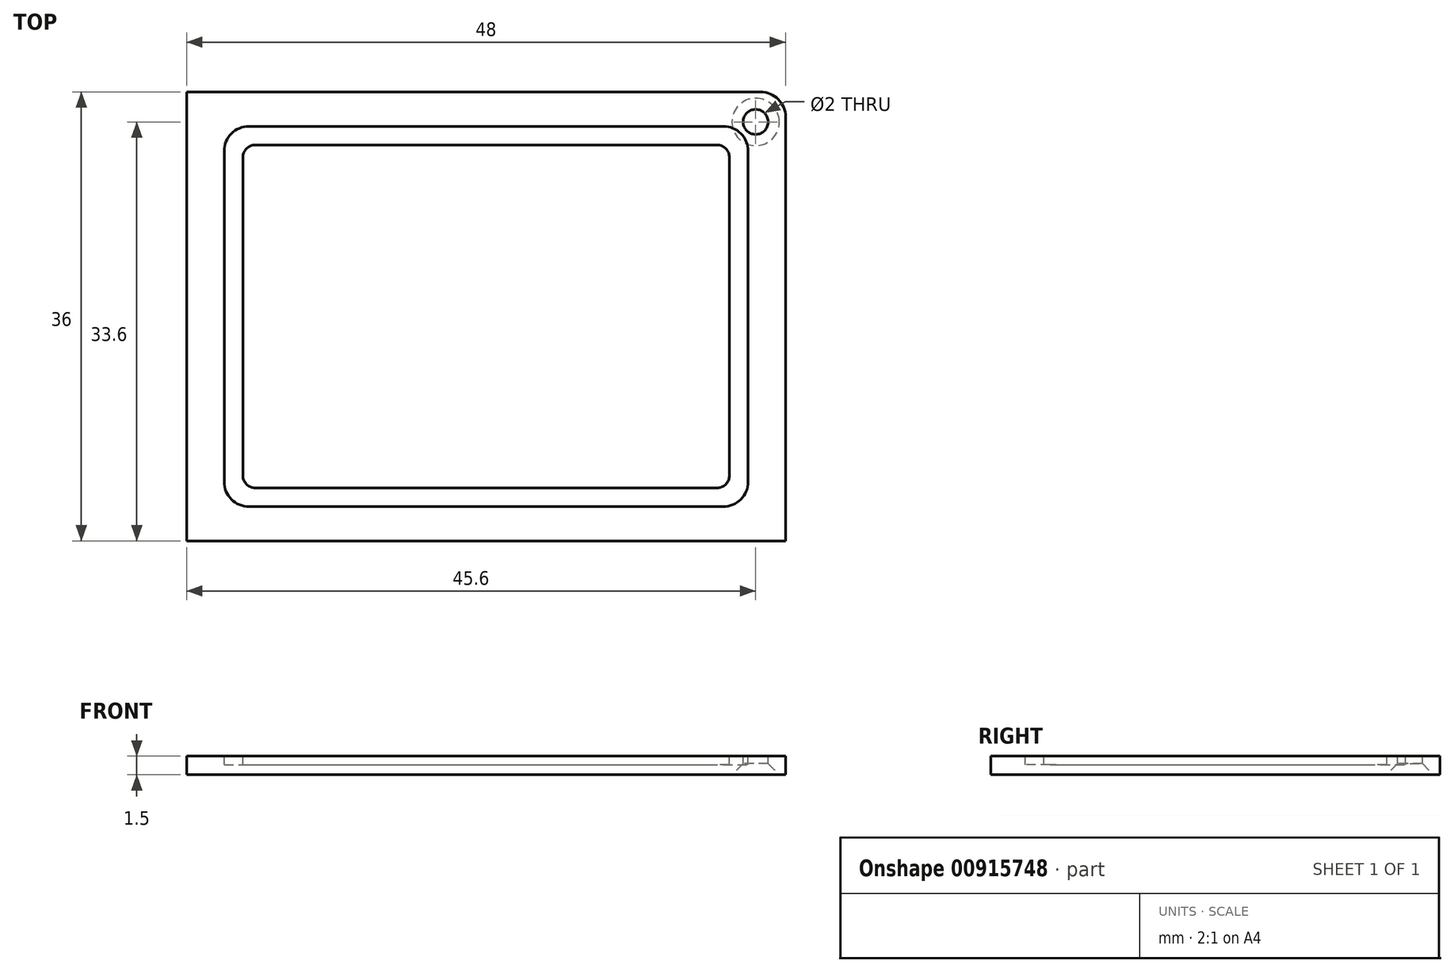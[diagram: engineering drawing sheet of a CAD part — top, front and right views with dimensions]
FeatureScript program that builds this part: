
annotation { "Feature Type Name" : "Feature", "Feature Type Description" : "" }
export const myFeature = defineFeature(function(context is Context, id is Id, definition is map)
    precondition{}
    {
        {
            var Q0;
            Q0=qCreatedBy(makeId("Top.planeOp"),FACE);
            var sketch = newSketch(context, id + "F0", { "sketchPlane" : qUnion([Q0])});
            skLineSegment(sketch, "E0.bottom", {"start": v(0, 0) * mm, "end": v(38, 0) * mm, "construction": true});
            skLineSegment(sketch, "E0.top", {"start": v(0, 26.5) * mm, "end": v(38, 26.5) * mm, "construction": true});
            skLineSegment(sketch, "E0.left", {"start": v(0, 0) * mm, "end": v(0, 26.5) * mm, "construction": true});
            skLineSegment(sketch, "E0.right", {"start": v(38, 0) * mm, "end": v(38, 26.5) * mm, "construction": true});
            skSolve(sketch);
        }
        {
            var Q0;
            Q0=qCreatedBy(makeId("Top.planeOp"),FACE);
            var sketch = newSketch(context, id + "F1", { "sketchPlane" : qUnion([Q0])});
            skLineSegment(sketch, "E1.bottom", {"start": v(-5, -4.75) * mm, "end": v(43, -4.75) * mm});
            skLineSegment(sketch, "E1.top", {"start": v(-5, 31.25) * mm, "end": v(43, 31.25) * mm});
            skLineSegment(sketch, "E1.left", {"start": v(-5, -4.75) * mm, "end": v(-5, 31.25) * mm});
            skLineSegment(sketch, "E1.right", {"start": v(43, -4.75) * mm, "end": v(43, 31.25) * mm});
            skSolve(sketch);
        }
        {
            var Q0;
            Q0=makeQuery(id+"F1.imprint","IMPRINT",FACE,{"disambiguationData":[TD([[makeQuery(id+"F1.imprint","IMPRINT",EDGE,{"derivedFrom":sQuery(id+"F1.wireOp",EDGE,"E1.bottom")}),1.0]])]});
            extrude(context, id + "F2", {"entities" : qUnion([Q0]), "depth" : 1.5 * mm, "offsetDistance" : 25 * mm});
        }
        {
            var Q0;
            Q0=makeQuery(id+"F2.opExtrude","CAP_FACE",FACE,{"disambiguationData":[OSD([sQuery(id+"F1.wireOp",EDGE,"E1.bottom"),sQuery(id+"F1.wireOp",EDGE,"E1.top"),sQuery(id+"F1.wireOp",EDGE,"E1.left"),sQuery(id+"F1.wireOp",EDGE,"E1.right")])],"isStart":false});
            var sketch = newSketch(context, id + "F3", { "sketchPlane" : qUnion([Q0])});
            skLineSegment(sketch, "E2.bottom", {"start": v(-0.5, -0.5) * mm, "end": v(38.5, -0.5) * mm});
            skLineSegment(sketch, "E2.top", {"start": v(-0.5, 27) * mm, "end": v(38.5, 27) * mm});
            skLineSegment(sketch, "E2.left", {"start": v(-0.5, -0.5) * mm, "end": v(-0.5, 27) * mm});
            skLineSegment(sketch, "E2.right", {"start": v(38.5, -0.5) * mm, "end": v(38.5, 27) * mm});
            skSolve(sketch);
        }
        {
            var Q0;
            Q0=makeQuery(id+"F3.imprint","IMPRINT",FACE,{"disambiguationData":[TD([[makeQuery(id+"F3.imprint","IMPRINT",EDGE,{"derivedFrom":sQuery(id+"F3.wireOp",EDGE,"E2.bottom")}),-1.0]])]});
            var sketch = newSketch(context, id + "F4", { "sketchPlane" : qUnion([Q0])});
            skLineSegment(sketch, "E3.0", {"start": v(-2, 28.5) * mm, "end": v(40, 28.5) * mm});
            skLineSegment(sketch, "E3.1", {"start": v(-2, -2) * mm, "end": v(-2, 28.5) * mm});
            skLineSegment(sketch, "E3.2", {"start": v(-2, -2) * mm, "end": v(40, -2) * mm});
            skLineSegment(sketch, "E3.3", {"start": v(40, -2) * mm, "end": v(40, 28.5) * mm});
            skSolve(sketch);
        }
        {
            var Q0;
            Q0=makeQuery(id+"F4.imprint","IMPRINT",FACE,{"disambiguationData":[TD([[makeQuery(id+"F4.imprint","IMPRINT",EDGE,{"derivedFrom":sQuery(id+"F4.wireOp",EDGE,"E3.0")}),1.0]])]});
            var sketch = newSketch(context, id + "F5", { "sketchPlane" : qUnion([Q0])});
            skCircle(sketch, "E4", {"center": v(40.6, 28.85) * mm, "radius": 1.9 * mm});
            skCircle(sketch, "E5", {"center": v(40.6, 28.85) * mm, "radius": 1 * mm});
            skSolve(sketch);
        }
        {
            var Q0;
            Q0=makeQuery(id+"F4.imprint","IMPRINT",FACE,{"disambiguationData":[TD([[makeQuery(id+"F4.imprint","IMPRINT",EDGE,{"derivedFrom":sQuery(id+"F4.wireOp",EDGE,"E3.0")}),-1.0]])]});
            extrude(context, id + "F6", {"entities" : qUnion([Q0]), "operationType" : NewBodyOperationType.REMOVE, "oppositeDirection" : true, "depth" : .7 * mm, "offsetDistance" : 25 * mm});
        }
        {
            var Q0;
            Q0=makeQuery(id+"F6.boolean.opBoolean","COPY",EDGE,{"derivedFrom":makeQuery(id+"F6.opExtrude","SWEPT_EDGE",EDGE,{"disambiguationData":[OSD([sQuery(id+"F4.wireOp",EDGE,"E3.0"),sQuery(id+"F4.wireOp",EDGE,"E3.3")])]})});
            var Q1;
            Q1=makeQuery(id+"F6.boolean.opBoolean","COPY",EDGE,{"derivedFrom":makeQuery(id+"F6.opExtrude","SWEPT_EDGE",EDGE,{"disambiguationData":[OSD([sQuery(id+"F4.wireOp",EDGE,"E3.2"),sQuery(id+"F4.wireOp",EDGE,"E3.3")])]})});
            var Q2;
            Q2=makeQuery(id+"F6.boolean.opBoolean","COPY",EDGE,{"derivedFrom":makeQuery(id+"F6.opExtrude","SWEPT_EDGE",EDGE,{"disambiguationData":[OSD([sQuery(id+"F4.wireOp",EDGE,"E3.0"),sQuery(id+"F4.wireOp",EDGE,"E3.1")])]})});
            var Q3;
            Q3=makeQuery(id+"F6.boolean.opBoolean","COPY",EDGE,{"derivedFrom":makeQuery(id+"F6.opExtrude","SWEPT_EDGE",EDGE,{"disambiguationData":[OSD([sQuery(id+"F4.wireOp",EDGE,"E3.1"),sQuery(id+"F4.wireOp",EDGE,"E3.2")])]})});
            fillet(context, id + "F7", {"entities" : qUnion([Q0, Q1, Q2, Q3]), "radius" : 2 * mm, "tangentPropagation" : true, "allowEdgeOverflow" : false});
        }
        {
            var Q0;
            Q0=makeQuery(id+"F6.boolean.opBoolean","COPY",EDGE,{"derivedFrom":makeQuery(id+"F6.opExtrude","SWEPT_EDGE",EDGE,{"disambiguationData":[OSD([sQuery(id+"F3.wireOp",EDGE,"E2.top"),sQuery(id+"F3.wireOp",EDGE,"E2.right")])]})});
            var Q1;
            Q1=makeQuery(id+"F6.boolean.opBoolean","COPY",EDGE,{"derivedFrom":makeQuery(id+"F6.opExtrude","SWEPT_EDGE",EDGE,{"disambiguationData":[OSD([sQuery(id+"F3.wireOp",EDGE,"E2.bottom"),sQuery(id+"F3.wireOp",EDGE,"E2.right")])]})});
            var Q2;
            Q2=makeQuery(id+"F6.boolean.opBoolean","COPY",EDGE,{"derivedFrom":makeQuery(id+"F6.opExtrude","SWEPT_EDGE",EDGE,{"disambiguationData":[OSD([sQuery(id+"F3.wireOp",EDGE,"E2.bottom"),sQuery(id+"F3.wireOp",EDGE,"E2.left")])]})});
            var Q3;
            Q3=makeQuery(id+"F6.boolean.opBoolean","COPY",EDGE,{"derivedFrom":makeQuery(id+"F6.opExtrude","SWEPT_EDGE",EDGE,{"disambiguationData":[OSD([sQuery(id+"F3.wireOp",EDGE,"E2.top"),sQuery(id+"F3.wireOp",EDGE,"E2.left")])]})});
            fillet(context, id + "F8", {"entities" : qUnion([Q0, Q1, Q2, Q3]), "radius" : 1 * mm, "tangentPropagation" : true, "allowEdgeOverflow" : false});
        }
        {
            var Q0;
            Q0=makeQuery(id+"F5.imprint","IMPRINT",FACE,{"disambiguationData":[TD([[makeQuery(id+"F5.imprint","IMPRINT",EDGE,{"derivedFrom":sQuery(id+"F5.wireOp",EDGE,"E5")}),1.0]])]});
            extrude(context, id + "F9", {"entities" : qUnion([Q0]), "operationType" : NewBodyOperationType.REMOVE, "oppositeDirection" : true, "depth" : 25 * mm, "offsetDistance" : 25 * mm});
        }
        {
            var Q0;
            Q0=makeQuery(id+"F9.boolean.opBoolean","INTERSECT",EDGE,{"derivedFrom":[makeQuery(id+"F2.opExtrude","CAP_FACE",FACE,{"disambiguationData":[OSD([sQuery(id+"F1.wireOp",EDGE,"E1.bottom"),sQuery(id+"F1.wireOp",EDGE,"E1.top"),sQuery(id+"F1.wireOp",EDGE,"E1.left"),sQuery(id+"F1.wireOp",EDGE,"E1.right")])],"isStart":true}),makeQuery(id+"F9.opExtrude","SWEPT_FACE",FACE,{"disambiguationData":[OSD([sQuery(id+"F5.wireOp",EDGE,"E5")])]})]});
            chamfer(context, id + "F10", {"entities" : qUnion([Q0]), "chamferType" : ChamferType.OFFSET_ANGLE, "width" : .9 * mm, "oppositeDirection" : false, "angle" : 45 * degree, "tangentPropagation" : true});
        }
        {
            var Q0;
            Q0=makeQuery(id+"F2.opExtrude","SWEPT_EDGE",EDGE,{"disambiguationData":[OSD([sQuery(id+"F1.wireOp",EDGE,"E1.top"),sQuery(id+"F1.wireOp",EDGE,"E1.right")])]});
            fillet(context, id + "F11", {"entities" : qUnion([Q0]), "radius" : 2 * mm, "tangentPropagation" : true, "allowEdgeOverflow" : false});
        }
    });
